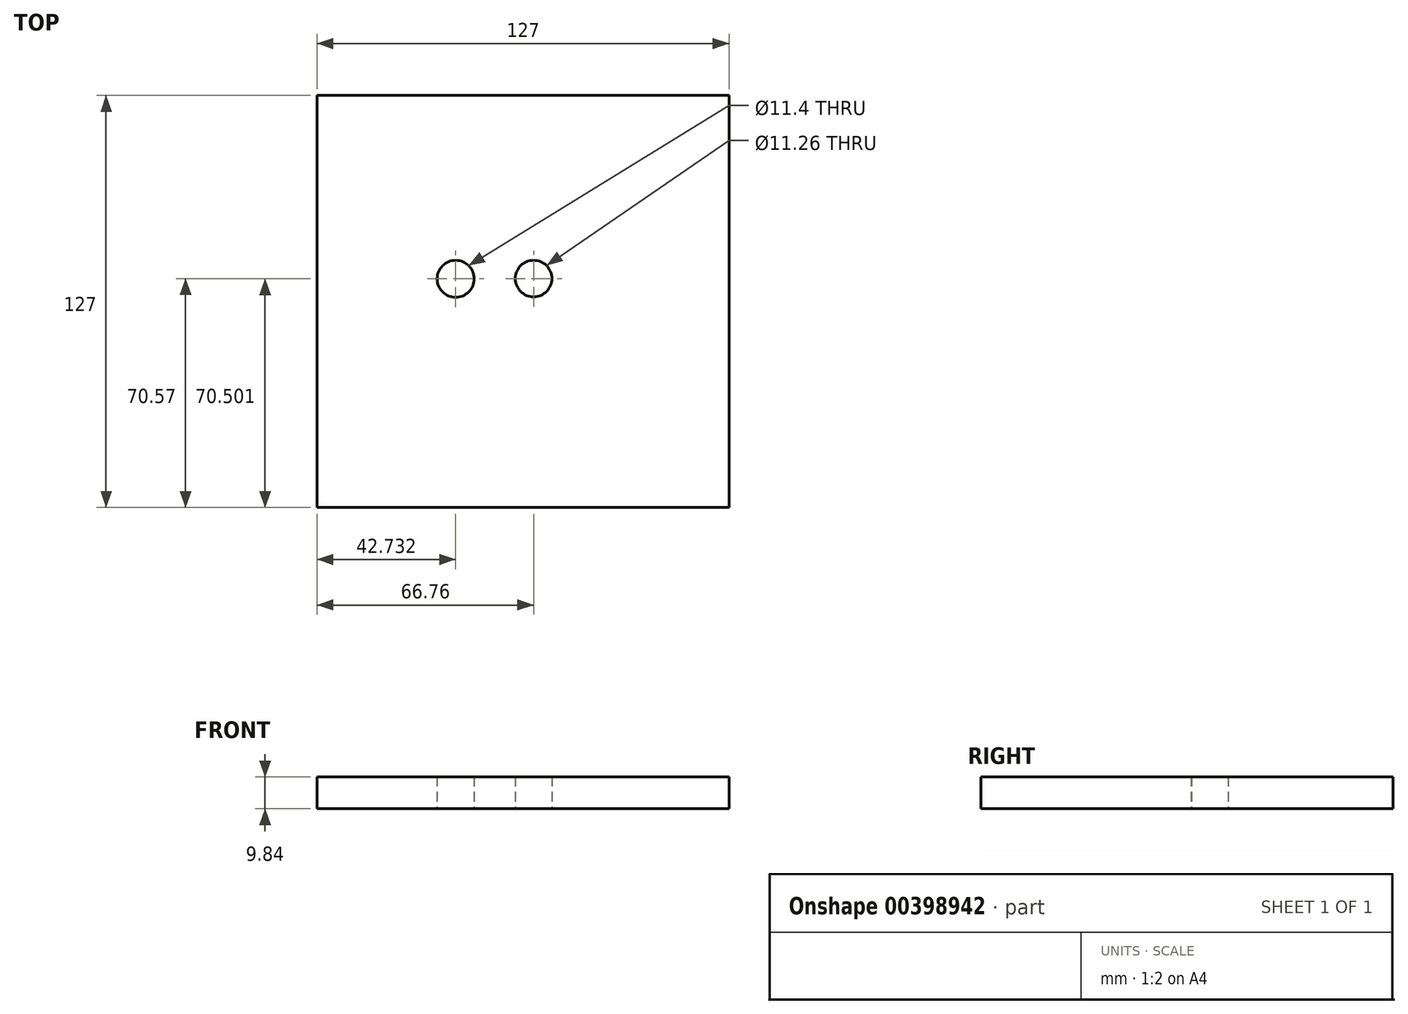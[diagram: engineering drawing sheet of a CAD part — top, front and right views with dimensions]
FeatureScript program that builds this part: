
annotation { "Feature Type Name" : "Feature", "Feature Type Description" : "" }
export const myFeature = defineFeature(function(context is Context, id is Id, definition is map)
    precondition{}
    {
        {
            var Q0;
            Q0=qCreatedBy(makeId("Top.planeOp"),FACE);
            var sketch = newSketch(context, id + "F0", { "sketchPlane" : qUnion([Q0])});
            skLineSegment(sketch, "E0.bottom", {"start": v(0, 0) * mm, "end": v(127, 0) * mm});
            skLineSegment(sketch, "E0.top", {"start": v(0, -127) * mm, "end": v(127, -127) * mm});
            skLineSegment(sketch, "E0.left", {"start": v(0, 0) * mm, "end": v(0, -127) * mm});
            skLineSegment(sketch, "E0.right", {"start": v(127, 0) * mm, "end": v(127, -127) * mm});
            skCircle(sketch, "E1", {"center": v(42.73, -56.5) * mm, "radius": 5.7 * mm});
            skCircle(sketch, "E2", {"center": v(66.76, -56.43) * mm, "radius": 5.63 * mm});
            skSolve(sketch);
        }
        {
            var Q0;
            Q0=makeQuery(id+"F0.imprint","IMPRINT",FACE,{"disambiguationData":[TD([[makeQuery(id+"F0.imprint","IMPRINT",EDGE,{"derivedFrom":sQuery(id+"F0.wireOp",EDGE,"E0.bottom")}),-1.0]])]});
            extrude(context, id + "F1", {"entities" : qUnion([Q0]), "depth" : 9.84 * mm, "offsetDistance" : 25.4 * mm});
        }
    });
